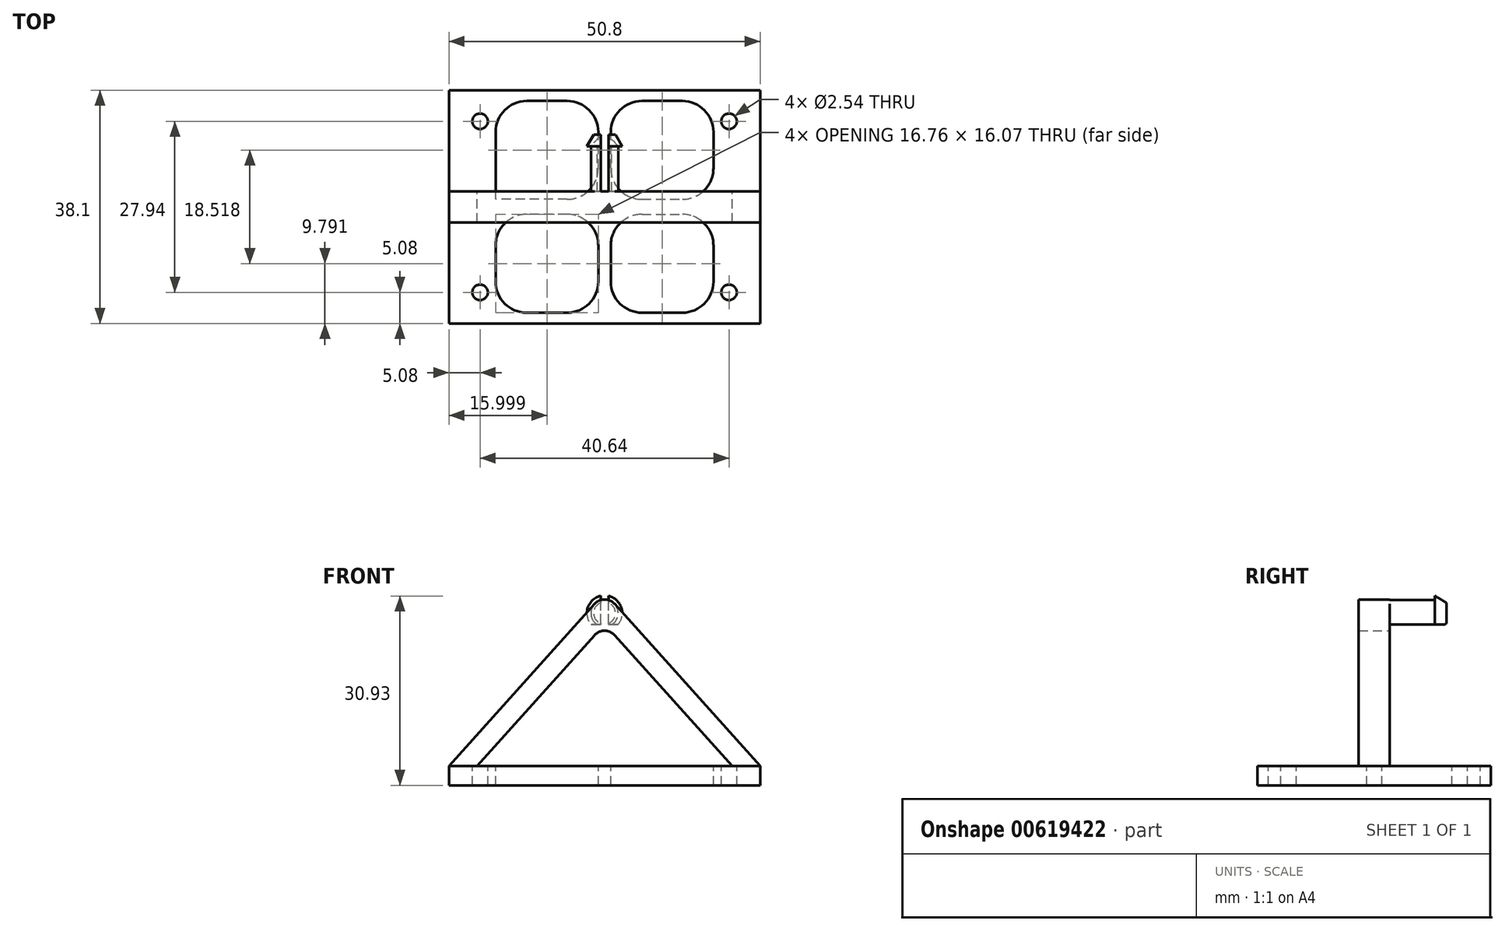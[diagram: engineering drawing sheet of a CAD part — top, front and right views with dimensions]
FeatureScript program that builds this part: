
annotation { "Feature Type Name" : "Feature", "Feature Type Description" : "" }
export const myFeature = defineFeature(function(context is Context, id is Id, definition is map)
    precondition{}
    {
        {
            var Q0;
            Q0=qCreatedBy(makeId("Top.planeOp"),FACE);
            var sketch = newSketch(context, id + "F0", { "sketchPlane" : qUnion([Q0])});
            skLineSegment(sketch, "E0.bottom", {"start": v(25.4, -19.05) * mm, "end": v(-25.4, -19.05) * mm});
            skLineSegment(sketch, "E0.top", {"start": v(25.4, 19.05) * mm, "end": v(-25.4, 19.05) * mm});
            skLineSegment(sketch, "E0.left", {"start": v(25.4, -19.05) * mm, "end": v(25.4, 19.05) * mm});
            skLineSegment(sketch, "E0.right", {"start": v(-25.4, -19.05) * mm, "end": v(-25.4, 19.05) * mm});
            skPoint(sketch, "E0.middle", {"position": v(0, 0) * mm});
            skSolve(sketch);
        }
        {
            var Q0;
            Q0 = qSketchRegion(id + "F0", true);
            extrude(context, id + "F1", {"entities" : qUnion([Q0]), "depth" : 3.17 * mm, "offsetDistance" : 25.4 * mm});
        }
        {
            var Q0;
            Q0=qCreatedBy(makeId("Front.planeOp"),FACE);
            var sketch = newSketch(context, id + "F2", { "sketchPlane" : qUnion([Q0])});
            skLineSegment(sketch, "E1", {"start": v(-20.83, 3.17) * mm, "end": v(-1.65, 24.52) * mm});
            skLineSegment(sketch, "E2", {"start": v(-1.65, 29.6) * mm, "end": v(-25.4, 3.17) * mm});
            skLineSegment(sketch, "E3", {"start": v(1.65, 24.52) * mm, "end": v(20.83, 3.17) * mm});
            skLineSegment(sketch, "E4", {"start": v(1.65, 29.6) * mm, "end": v(25.4, 3.17) * mm});
            skLineSegment(sketch, "E5", {"start": v(20.83, 3.18) * mm, "end": v(25.4, 3.17) * mm});
            skLineSegment(sketch, "E6", {"start": v(-20.83, 3.18) * mm, "end": v(-25.4, 3.17) * mm});
            skPoint(sketch, "E7.visualSharp", {"position": v(0, 38.08) * mm});
            skPoint(sketch, "E8.visualSharp", {"position": v(0, 31.8) * mm});
            skPoint(sketch, "E9.visualSharp", {"position": v(0, 26.36) * mm});
            skArc(sketch, "E9.filletArc", {"start": v(1.65, 24.52) * mm, "mid": v(0, 25.25) * mm, "end": v(-1.65, 24.52) * mm});
            skPoint(sketch, "E10.visualSharp", {"position": v(0, 31.45) * mm});
            skArc(sketch, "E10.filletArc", {"start": v(1.65, 29.6) * mm, "mid": v(0, 30.34) * mm, "end": v(-1.65, 29.6) * mm});
            skSolve(sketch);
        }
        {
            var Q0;
            Q0=makeQuery(id+"F2.imprint","IMPRINT",FACE,{"disambiguationData":[TD([[makeQuery(id+"F2.imprint","IMPRINT",EDGE,{"derivedFrom":sQuery(id+"F2.wireOp",EDGE,"E1")}),1.0]])]});
            extrude(context, id + "F3", {"entities" : qUnion([Q0]), "operationType" : NewBodyOperationType.ADD, "endBound" : BoundingType.SYMMETRIC, "depth" : 5.08 * mm, "offsetDistance" : 25.4 * mm});
        }
        {
            var Q0;
            Q0=makeQuery(id+"F1.opExtrude","CAP_FACE",FACE,{"disambiguationData":[OSD([sQuery(id+"F0.wireOp",EDGE,"E0.bottom"),sQuery(id+"F0.wireOp",EDGE,"E0.top"),sQuery(id+"F0.wireOp",EDGE,"E0.left"),sQuery(id+"F0.wireOp",EDGE,"E0.right")])],"isStart":false});
            var sketch = newSketch(context, id + "F4", { "sketchPlane" : qUnion([Q0])});
            skCircle(sketch, "E11", {"center": v(-20.32, 13.97) * mm, "radius": 1.27 * mm});
            skCircle(sketch, "E12.MirrorC", {"center": v(20.32, 13.97) * mm, "radius": 1.27 * mm});
            skCircle(sketch, "E13.MirrorC", {"center": v(-20.32, -13.97) * mm, "radius": 1.27 * mm});
            skCircle(sketch, "E14.MirrorC", {"center": v(20.32, -13.97) * mm, "radius": 1.27 * mm});
            skSolve(sketch);
        }
        {
            var Q0;
            Q0 = qSketchRegion(id + "F4", true);
            extrude(context, id + "F5", {"entities" : qUnion([Q0]), "operationType" : NewBodyOperationType.REMOVE, "endBound" : BoundingType.THROUGH_ALL, "oppositeDirection" : true, "depth" : 25.4 * mm, "offsetDistance" : 25.4 * mm});
        }
        {
            var Q0;
            Q0=makeQuery(id+"F3.opExtrude","CAP_FACE",FACE,{"disambiguationData":[OSD([sQuery(id+"F2.wireOp",EDGE,"E1"),sQuery(id+"F2.wireOp",EDGE,"E2"),sQuery(id+"F2.wireOp",EDGE,"E3"),sQuery(id+"F2.wireOp",EDGE,"E4"),sQuery(id+"F2.wireOp",EDGE,"E5"),sQuery(id+"F2.wireOp",EDGE,"E6"),sQuery(id+"F2.wireOp",EDGE,"E7.filletArc"),sQuery(id+"F2.wireOp",EDGE,"E8.filletArc")])],"isStart":true});
            var sketch = newSketch(context, id + "F6", { "sketchPlane" : qUnion([Q0])});
            skCircle(sketch, "E15", {"center": v(0, 28.12) * mm, "radius": 2.22 * mm});
            skPoint(sketch, "E16", {"position": v(0, 30.34) * mm});
            skSolve(sketch);
        }
        {
            var Q0;
            Q0=makeQuery(id+"F6.imprint","IMPRINT",FACE,{"disambiguationData":[TD([[makeQuery(id+"F6.imprint","IMPRINT",EDGE,{"derivedFrom":sQuery(id+"F6.wireOp",EDGE,"E15")}),1.0]])]});
            extrude(context, id + "F7", {"entities" : qUnion([Q0]), "operationType" : NewBodyOperationType.ADD, "depth" : 7.37 * mm, "offsetDistance" : 25.4 * mm});
        }
        {
            var Q0;
            Q0=makeQuery(id+"F7.opExtrude","CAP_FACE",FACE,{"disambiguationData":[OSD([sQuery(id+"F6.wireOp",EDGE,"E15")])],"isStart":false});
            var sketch = newSketch(context, id + "F8", { "sketchPlane" : qUnion([Q0])});
            skCircle(sketch, "E17", {"center": v(0, 28.12) * mm, "radius": 2.88 * mm});
            skSolve(sketch);
        }
        {
            var Q0;
            Q0 = qSketchRegion(id + "F8", true);
            extrude(context, id + "F9", {"entities" : qUnion([Q0]), "operationType" : NewBodyOperationType.ADD, "depth" : 1.9 * mm, "offsetDistance" : 25.4 * mm, "hasDraft" : true, "draftAngle" : 30 * degree, "draftPullDirection" : true});
        }
        {
            var Q0;
            Q0=makeQuery(id+"F1.opExtrude","CAP_FACE",FACE,{"disambiguationData":[OSD([sQuery(id+"F0.wireOp",EDGE,"E0.bottom"),sQuery(id+"F0.wireOp",EDGE,"E0.top"),sQuery(id+"F0.wireOp",EDGE,"E0.left"),sQuery(id+"F0.wireOp",EDGE,"E0.right")])],"isStart":false});
            var sketch = newSketch(context, id + "F10", { "sketchPlane" : qUnion([Q0])});
            skLineSegment(sketch, "E18.bottom", {"start": v(-1.02, 1.23) * mm, "end": v(-17.78, 1.23) * mm});
            skLineSegment(sketch, "E18.top", {"start": v(-1.02, 17.3) * mm, "end": v(-17.78, 17.3) * mm});
            skLineSegment(sketch, "E18.left", {"start": v(-1.02, 1.23) * mm, "end": v(-1.02, 17.3) * mm});
            skLineSegment(sketch, "E18.right", {"start": v(-17.78, 1.23) * mm, "end": v(-17.78, 17.3) * mm});
            skLineSegment(sketch, "E19.MirrorCS", {"start": v(17.78, 1.23) * mm, "end": v(17.78, 17.3) * mm});
            skLineSegment(sketch, "E20.MirrorCS", {"start": v(1.02, 17.3) * mm, "end": v(17.78, 17.3) * mm});
            skLineSegment(sketch, "E21.MirrorCS", {"start": v(1.02, 1.23) * mm, "end": v(17.78, 1.23) * mm});
            skLineSegment(sketch, "E22.MirrorCS", {"start": v(1.02, 1.23) * mm, "end": v(1.02, 17.3) * mm});
            skLineSegment(sketch, "E23.MirrorCS", {"start": v(1.02, -1.23) * mm, "end": v(17.78, -1.23) * mm});
            skLineSegment(sketch, "E24.MirrorCS", {"start": v(-1.02, -1.23) * mm, "end": v(-17.78, -1.23) * mm});
            skLineSegment(sketch, "E25.MirrorCS", {"start": v(1.02, -17.3) * mm, "end": v(17.78, -17.3) * mm});
            skLineSegment(sketch, "E26.MirrorCS", {"start": v(1.02, -1.23) * mm, "end": v(1.02, -17.3) * mm});
            skLineSegment(sketch, "E27.MirrorCS", {"start": v(-1.02, -1.23) * mm, "end": v(-1.02, -17.3) * mm});
            skLineSegment(sketch, "E28.MirrorCS", {"start": v(17.78, -1.23) * mm, "end": v(17.78, -17.3) * mm});
            skLineSegment(sketch, "E29.MirrorCS", {"start": v(-1.02, -17.3) * mm, "end": v(-17.78, -17.3) * mm});
            skLineSegment(sketch, "E30.MirrorCS", {"start": v(-17.78, -1.23) * mm, "end": v(-17.78, -17.3) * mm});
            skSolve(sketch);
        }
        {
            var Q0;
            Q0 = qSketchRegion(id + "F10", true);
            extrude(context, id + "F11", {"entities" : qUnion([Q0]), "operationType" : NewBodyOperationType.REMOVE, "oppositeDirection" : true, "depth" : 25.4 * mm, "offsetDistance" : 25.4 * mm});
        }
        {
            var Q0;
            Q0=makeQuery(id+"F11.boolean.opBoolean","COPY",EDGE,{"derivedFrom":makeQuery(id+"F11.opExtrude","SWEPT_EDGE",EDGE,{"disambiguationData":[OSD([sQuery(id+"F10.wireOp",EDGE,"E23.MirrorCS"),sQuery(id+"F10.wireOp",EDGE,"E26.MirrorCS")])]})});
            var Q1;
            Q1=makeQuery(id+"F11.boolean.opBoolean","COPY",EDGE,{"derivedFrom":makeQuery(id+"F11.opExtrude","SWEPT_EDGE",EDGE,{"disambiguationData":[OSD([sQuery(id+"F10.wireOp",EDGE,"E24.MirrorCS"),sQuery(id+"F10.wireOp",EDGE,"E27.MirrorCS")])]})});
            var Q2;
            Q2=makeQuery(id+"F11.boolean.opBoolean","COPY",EDGE,{"derivedFrom":makeQuery(id+"F11.opExtrude","SWEPT_EDGE",EDGE,{"disambiguationData":[OSD([sQuery(id+"F10.wireOp",EDGE,"E18.left"),sQuery(id+"F10.wireOp",EDGE,"E18.bottom")])]})});
            var Q3;
            Q3=makeQuery(id+"F11.boolean.opBoolean","COPY",EDGE,{"derivedFrom":makeQuery(id+"F11.opExtrude","SWEPT_EDGE",EDGE,{"disambiguationData":[OSD([sQuery(id+"F10.wireOp",EDGE,"E22.MirrorCS"),sQuery(id+"F10.wireOp",EDGE,"E21.MirrorCS")])]})});
            var Q4;
            Q4=makeQuery(id+"F11.boolean.opBoolean","COPY",EDGE,{"derivedFrom":makeQuery(id+"F11.opExtrude","SWEPT_EDGE",EDGE,{"disambiguationData":[OSD([sQuery(id+"F10.wireOp",EDGE,"E29.MirrorCS"),sQuery(id+"F10.wireOp",EDGE,"E27.MirrorCS")])]})});
            var Q5;
            Q5=makeQuery(id+"F11.boolean.opBoolean","COPY",EDGE,{"derivedFrom":makeQuery(id+"F11.opExtrude","SWEPT_EDGE",EDGE,{"disambiguationData":[OSD([sQuery(id+"F10.wireOp",EDGE,"E26.MirrorCS"),sQuery(id+"F10.wireOp",EDGE,"E25.MirrorCS")])]})});
            var Q6;
            Q6=makeQuery(id+"F11.boolean.opBoolean","COPY",EDGE,{"derivedFrom":makeQuery(id+"F11.opExtrude","SWEPT_EDGE",EDGE,{"disambiguationData":[OSD([sQuery(id+"F10.wireOp",EDGE,"E25.MirrorCS"),sQuery(id+"F10.wireOp",EDGE,"E28.MirrorCS")])]})});
            var Q7;
            Q7=makeQuery(id+"F11.boolean.opBoolean","COPY",EDGE,{"derivedFrom":makeQuery(id+"F11.opExtrude","SWEPT_EDGE",EDGE,{"disambiguationData":[OSD([sQuery(id+"F10.wireOp",EDGE,"E23.MirrorCS"),sQuery(id+"F10.wireOp",EDGE,"E28.MirrorCS")])]})});
            var Q8;
            Q8=makeQuery(id+"F11.boolean.opBoolean","COPY",EDGE,{"derivedFrom":makeQuery(id+"F11.opExtrude","SWEPT_EDGE",EDGE,{"disambiguationData":[OSD([sQuery(id+"F10.wireOp",EDGE,"E19.MirrorCS"),sQuery(id+"F10.wireOp",EDGE,"E20.MirrorCS")])]})});
            var Q9;
            Q9=makeQuery(id+"F11.boolean.opBoolean","COPY",EDGE,{"derivedFrom":makeQuery(id+"F11.opExtrude","SWEPT_EDGE",EDGE,{"disambiguationData":[OSD([sQuery(id+"F10.wireOp",EDGE,"E19.MirrorCS"),sQuery(id+"F10.wireOp",EDGE,"E21.MirrorCS")])]})});
            var Q10;
            Q10=makeQuery(id+"F11.boolean.opBoolean","COPY",EDGE,{"derivedFrom":makeQuery(id+"F11.opExtrude","SWEPT_EDGE",EDGE,{"disambiguationData":[OSD([sQuery(id+"F10.wireOp",EDGE,"E22.MirrorCS"),sQuery(id+"F10.wireOp",EDGE,"E20.MirrorCS")])]})});
            var Q11;
            Q11=makeQuery(id+"F11.boolean.opBoolean","COPY",EDGE,{"derivedFrom":makeQuery(id+"F11.opExtrude","SWEPT_EDGE",EDGE,{"disambiguationData":[OSD([sQuery(id+"F10.wireOp",EDGE,"E18.left"),sQuery(id+"F10.wireOp",EDGE,"E18.top")])]})});
            var Q12;
            Q12=makeQuery(id+"F11.boolean.opBoolean","COPY",EDGE,{"derivedFrom":makeQuery(id+"F11.opExtrude","SWEPT_EDGE",EDGE,{"disambiguationData":[OSD([sQuery(id+"F10.wireOp",EDGE,"E18.right"),sQuery(id+"F10.wireOp",EDGE,"E18.bottom")])]})});
            var Q13;
            Q13=makeQuery(id+"F11.boolean.opBoolean","COPY",EDGE,{"derivedFrom":makeQuery(id+"F11.opExtrude","SWEPT_EDGE",EDGE,{"disambiguationData":[OSD([sQuery(id+"F10.wireOp",EDGE,"E18.right"),sQuery(id+"F10.wireOp",EDGE,"E18.top")])]})});
            var Q14;
            Q14=makeQuery(id+"F11.boolean.opBoolean","COPY",EDGE,{"derivedFrom":makeQuery(id+"F11.opExtrude","SWEPT_EDGE",EDGE,{"disambiguationData":[OSD([sQuery(id+"F10.wireOp",EDGE,"E30.MirrorCS"),sQuery(id+"F10.wireOp",EDGE,"E29.MirrorCS")])]})});
            var Q15;
            Q15=makeQuery(id+"F11.boolean.opBoolean","COPY",EDGE,{"derivedFrom":makeQuery(id+"F11.opExtrude","SWEPT_EDGE",EDGE,{"disambiguationData":[OSD([sQuery(id+"F10.wireOp",EDGE,"E24.MirrorCS"),sQuery(id+"F10.wireOp",EDGE,"E30.MirrorCS")])]})});
            fillet(context, id + "F12", {"entities" : qUnion([Q0, Q1, Q2, Q3, Q4, Q5, Q6, Q7, Q8, Q9, Q10, Q11, Q12, Q13, Q14, Q15]), "radius" : 5.08 * mm, "tangentPropagation" : true, "allowEdgeOverflow" : false});
        }
        {
            var Q0;
            Q0=makeQuery(id+"F9.opExtrude","CAP_FACE",FACE,{"disambiguationData":[OSD([sQuery(id+"F8.wireOp",EDGE,"E17")])],"isStart":false});
            var sketch = newSketch(context, id + "F13", { "sketchPlane" : qUnion([Q0])});
            skLineSegment(sketch, "E31.bottom", {"start": v(-0.64, 22) * mm, "end": v(0.64, 22) * mm});
            skLineSegment(sketch, "E31.top", {"start": v(-0.64, 34.24) * mm, "end": v(0.64, 34.24) * mm});
            skLineSegment(sketch, "E31.left", {"start": v(-0.64, 22) * mm, "end": v(-0.64, 34.24) * mm});
            skLineSegment(sketch, "E31.right", {"start": v(0.64, 22) * mm, "end": v(0.64, 34.24) * mm});
            skPoint(sketch, "E31.middle", {"position": v(0, 28.12) * mm});
            skSolve(sketch);
        }
        {
            var Q0;
            Q0 = qSketchRegion(id + "F13", true);
            var Q1;
            Q1=makeQuery(id+"F3.opExtrude","CAP_FACE",FACE,{"disambiguationData":[OSD([sQuery(id+"F2.wireOp",EDGE,"E1"),sQuery(id+"F2.wireOp",EDGE,"E2"),sQuery(id+"F2.wireOp",EDGE,"E3"),sQuery(id+"F2.wireOp",EDGE,"E4"),sQuery(id+"F2.wireOp",EDGE,"E5"),sQuery(id+"F2.wireOp",EDGE,"E6"),sQuery(id+"F2.wireOp",EDGE,"E9.filletArc"),sQuery(id+"F2.wireOp",EDGE,"E10.filletArc")])],"isStart":true});
            extrude(context, id + "F14", {"entities" : qUnion([Q0]), "operationType" : NewBodyOperationType.REMOVE, "endBound" : BoundingType.UP_TO_SURFACE, "oppositeDirection" : true, "depth" : 25.4 * mm, "endBoundEntityFace" : qUnion([Q1]), "offsetDistance" : 25.4 * mm});
        }
        {
            var Q0;
            Q0=makeQuery(id+"F1.opExtrude","CAP_FACE",FACE,{"disambiguationData":[OSD([sQuery(id+"F0.wireOp",EDGE,"E0.bottom"),sQuery(id+"F0.wireOp",EDGE,"E0.top"),sQuery(id+"F0.wireOp",EDGE,"E0.left"),sQuery(id+"F0.wireOp",EDGE,"E0.right")])],"isStart":false});
            var sketch = newSketch(context, id + "F15", { "sketchPlane" : qUnion([Q0])});
            skLineSegment(sketch, "E32.bottom", {"start": v(-2.28, 2.54) * mm, "end": v(2.3, 2.54) * mm});
            skLineSegment(sketch, "E32.top", {"start": v(-2.28, 11.86) * mm, "end": v(2.3, 11.86) * mm});
            skLineSegment(sketch, "E32.left", {"start": v(-2.28, 2.54) * mm, "end": v(-2.28, 11.86) * mm});
            skLineSegment(sketch, "E32.right", {"start": v(2.3, 2.54) * mm, "end": v(2.3, 11.86) * mm});
            skSolve(sketch);
        }
        {
            var Q0;
            Q0 = qSketchRegion(id + "F15", true);
            var Q1;
            Q1=makeQuery(id+"F14.boolean.opBoolean","INTERSECT",VERTEX,{"disambiguationData":[OD(1.0)],"derivedFrom":[makeQuery(id+"F7.boolean.opBoolean","MERGE",FACE,{"derivedFrom":[makeQuery(id+"F3.opExtrude","SWEPT_FACE",FACE,{"disambiguationData":[OSD([sQuery(id+"F2.wireOp",EDGE,"E10.filletArc")])]}),makeQuery(id+"F7.opExtrude","SWEPT_FACE",FACE,{"disambiguationData":[OSD([sQuery(id+"F6.wireOp",EDGE,"E15")])]})]}),makeQuery(id+"F9.opExtrude","CAP_FACE",FACE,{"disambiguationData":[OSD([sQuery(id+"F8.wireOp",EDGE,"E17")])],"isStart":true}),makeQuery(id+"F14.opExtrude","SWEPT_FACE",FACE,{"disambiguationData":[OSD([sQuery(id+"F13.wireOp",EDGE,"E31.left")])]})]});
            extrude(context, id + "F16", {"entities" : qUnion([Q0]), "operationType" : NewBodyOperationType.REMOVE, "endBound" : BoundingType.UP_TO_VERTEX, "depth" : 25.4 * mm, "endBoundEntityVertex" : qUnion([Q1]), "hasOffset" : true, "offsetDistance" : 0.25 * mm, "offsetOppositeDirection" : true});
        }
    });
